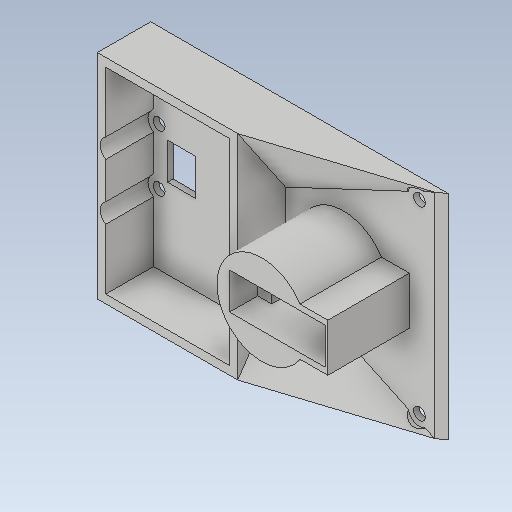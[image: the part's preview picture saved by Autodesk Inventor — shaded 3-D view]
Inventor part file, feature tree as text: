
AUTODESK INVENTOR PART (.ipt)
format: ipt  version: 2020 (Build 240168000, 168)  size: 294,400 bytes
history: native  units: mm
features: sketch x13, reference x13, extrude x10, other x6, loft x2, projected_geometry x2, plane x1, hole x1
ambient origin geometry x8: Origin, YZ Plane, XZ Plane, XY Plane, X Axis, Y Axis, Z Axis, Center Point
bodies: Solid1 (feature_tree)
feature tree (48):
  extrude  "Extrusion1"  Depth=76.0mm TaperAngle=0.0deg
  extrude  "Extrusion2"  Depth=3.0mm
  extrude  "Extrusion3"  Depth=3.0mm
  sketch  "3D Sketch1"
  sketch  "Sketch4"  dims[d8=3.0mm d9=17.0mm d10=0.0mm]
  loft  "Loft1"
  loft  "Loft2"
  extrude  "Extrusion5"  TaperAngle=0.0deg  [1 undecoded]
  extrude  "Extrusion6"  TaperAngle=0.0deg  [1 undecoded]
  sketch  "Sketch8"  dims[d17=0.0mm d18=90.0deg d19=0.0mm d20=90.0deg]
  plane  "Work Plane1"
  extrude  "Extrusion7"  Depth=13.0mm
  hole  "Hole1"  [1 undecoded]
  extrude  "Extrusion8"  Depth=6.0mm
  extrude  "Extrusion9"  Depth=2.0mm
  extrude  "Extrusion10"  Depth=19.0mm TaperAngle=0.0deg
  extrude  "Extrusion12"  Depth=0.5mm
  sketch  "Sketch1"  dims[d0=2.0mm d1=0.0mm d2=76.0mm d3=0.0mm]
  reference  "Reference1"
  sketch  "Sketch2"  dims[d4=50.0mm d5=3.0mm]
  reference  "Reference2"
  sketch  "Sketch3"  dims[d6=3.0mm d7=3.0mm]
  projected_geometry  "Projected Loop1"
  projected_geometry  "Projected Loop2"
  sketch  "Sketch6"  dims[d11=25.0mm d12=25.0mm]
  sketch  "Sketch7"  dims[d13=0.0mm d14=90.0deg d15=0.0mm d16=90.0deg]
  reference  "Reference11"
  reference  "Reference12"
  reference  "Reference13"
  reference  "Reference14"
  reference  "Reference15"
  sketch  "Sketch9"  dims[d25=24.0mm d26=13.0mm]
  reference  "Reference16"
  reference  "Reference17"
  sketch  "Sketch10"  dims[d27=15.0mm d29=19.0mm d30=0.0mm]
  sketch  "Sketch11"  dims[d31=6.0mm d32=6.0mm]
  reference  "Reference18"
  reference  "Reference19"
  reference  "Reference20"
  reference  "Reference21"
  sketch  "Sketch12"  dims[d33=2.0mm d34=2.0mm]
  sketch  "Sketch15"  dims[d35=32.0mm d36=19.0mm d37=0.0mm d38=0.5mm d39=0.5mm d40=4.75mm d41=0.0mm d42=1.0mm d43=6.0mm d44=4.0mm d45=2.0mm d46=90.0deg d47=5.0mm d48=20.594885mm d49=3.5mm d50=9.0mm d51=14.0mm d52=3.0mm d53=0.0mm d54=0.0mm d55=10.0mm d56=0.0mm d57=8.0mm d58=8.0mm d59=8.0mm d60=8.0mm d61=10.0mm d62=0.0mm d73=10.0mm d74=13.0mm d75=5.0mm d76=4.0mm d77=14.0mm d78=21.0mm d79=10.0mm d80=0.0mm]
  other  "<userpath>\Desktop\3d\scanning-robot\Assembly1.iam"
  other  "Assembly1.iam"
  other  "base:1"
  other  "Tower Pro MG90S Micro servo:3"
  other  "Вал последний с чем то:1"
  other  "Крышка корпуса:1"
note: 3 required parameter values undecoded (feature->parameter linkage not recoverable at this tier; creation-order binding heuristic only, values carry confidence <= 0.55)
